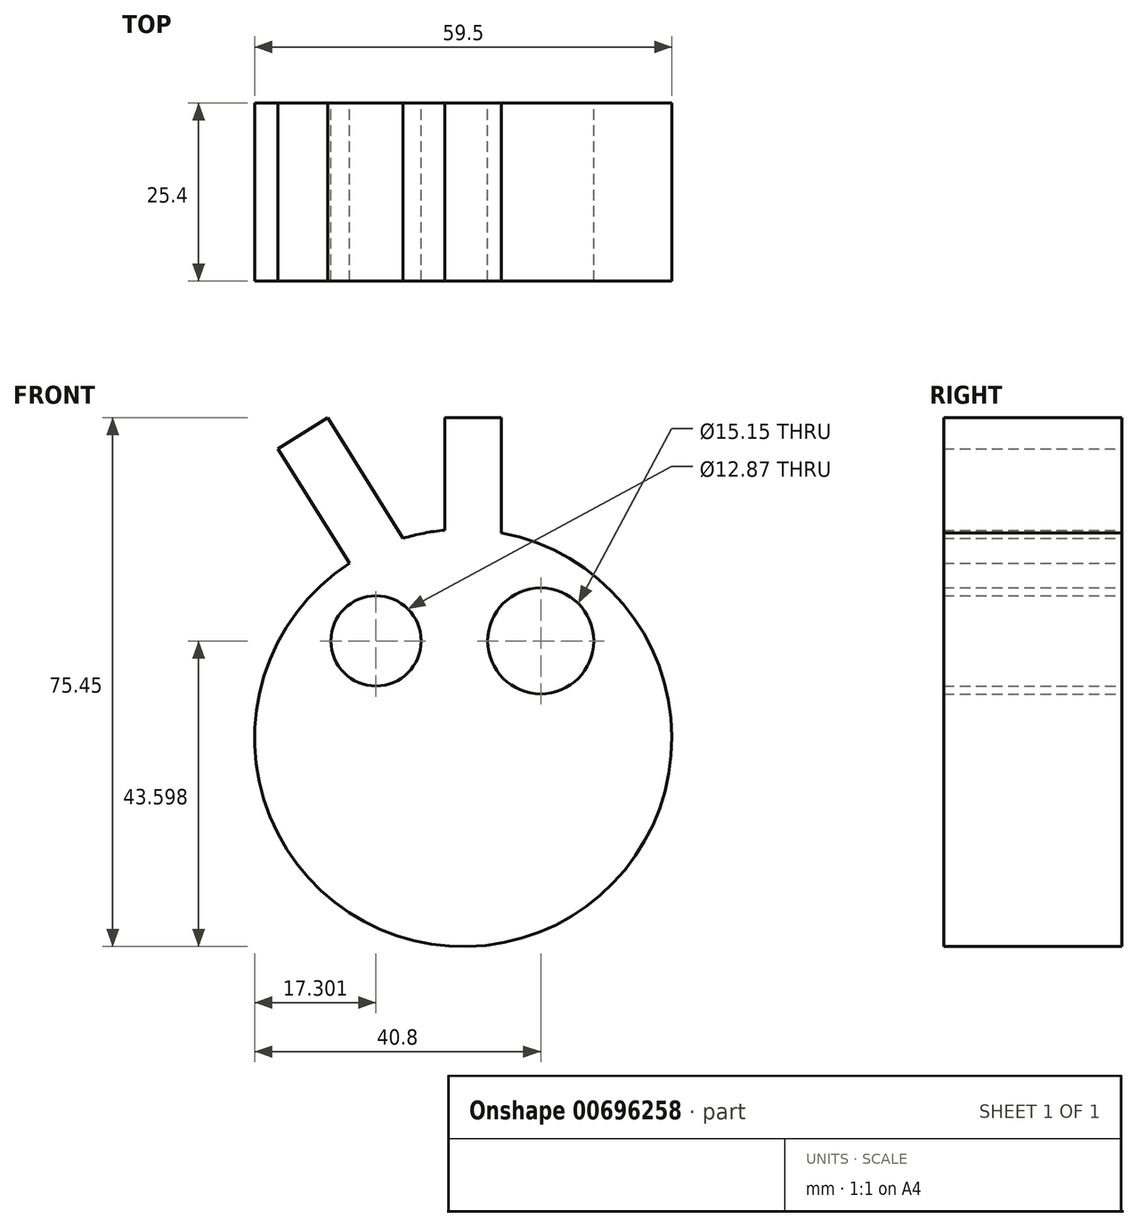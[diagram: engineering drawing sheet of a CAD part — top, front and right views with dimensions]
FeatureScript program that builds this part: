
annotation { "Feature Type Name" : "Feature", "Feature Type Description" : "" }
export const myFeature = defineFeature(function(context is Context, id is Id, definition is map)
    precondition{}
    {
        {
            var Q0;
            Q0=qCreatedBy(makeId("Front.planeOp"),FACE);
            var sketch = newSketch(context, id + "F0", { "sketchPlane" : qUnion([Q0])});
            skCircle(sketch, "E0", {"center": v(0, 0) * mm, "radius": 29.75 * mm});
            skLineSegment(sketch, "E1", {"start": v(-16.23, 24.94) * mm, "end": v(-26.44, 41.26) * mm});
            skLineSegment(sketch, "E2", {"start": v(-26.44, 41.26) * mm, "end": v(-19.35, 45.7) * mm});
            skLineSegment(sketch, "E3", {"start": v(-19.35, 45.7) * mm, "end": v(-8.58, 28.49) * mm});
            skLineSegment(sketch, "E4", {"start": v(-8.58, 28.49) * mm, "end": v(-19.35, 45.7) * mm});
            skLineSegment(sketch, "E5", {"start": v(-2.63, 29.64) * mm, "end": v(-2.63, 45.7) * mm});
            skLineSegment(sketch, "E6", {"start": v(-2.63, 45.7) * mm, "end": v(5.46, 45.7) * mm});
            skLineSegment(sketch, "E7", {"start": v(5.46, 45.7) * mm, "end": v(5.46, 29.25) * mm});
            skLineSegment(sketch, "E8", {"start": v(5.46, 29.25) * mm, "end": v(5.46, 45.7) * mm});
            skCircle(sketch, "E9", {"center": v(-12.45, 13.85) * mm, "radius": 6.43 * mm});
            skCircle(sketch, "E10", {"center": v(11.05, 13.85) * mm, "radius": 7.57 * mm});
            skArc(sketch, "E11", {"start": v(-10.77, -11.33) * mm, "mid": v(1.19, -20.75) * mm, "end": v(13.57, -11.89) * mm});
            skSolve(sketch);
        }
        {
            var Q0;
            Q0 = qSketchRegion(id + "F0", true);
            extrude(context, id + "F1", {"entities" : qUnion([Q0]), "depth" : 25.4 * mm, "offsetDistance" : 25.4 * mm});
        }
        {
            var Q0;
            Q0=qCreatedBy(makeId("Front.planeOp"),FACE);
            var sketch = newSketch(context, id + "F2", { "sketchPlane" : qUnion([Q0])});
            skLineSegment(sketch, "E12.bottom", {"start": v(-9.93, -9.1) * mm, "end": v(12.45, -9.1) * mm});
            skLineSegment(sketch, "E12.top", {"start": v(-9.93, -12.45) * mm, "end": v(12.45, -12.45) * mm});
            skLineSegment(sketch, "E12.left", {"start": v(-9.93, -9.1) * mm, "end": v(-9.93, -12.45) * mm});
            skLineSegment(sketch, "E12.right", {"start": v(12.45, -9.1) * mm, "end": v(12.45, -12.45) * mm});
            skLineSegment(sketch, "E13.bottom", {"start": v(-6.3, -9.1) * mm, "end": v(7.13, -9.1) * mm});
            skLineSegment(sketch, "E13.top", {"start": v(-6.3, -12.45) * mm, "end": v(7.13, -12.45) * mm});
            skLineSegment(sketch, "E13.left", {"start": v(-6.3, -9.1) * mm, "end": v(-6.3, -12.45) * mm});
            skLineSegment(sketch, "E13.right", {"start": v(7.13, -9.1) * mm, "end": v(7.13, -12.45) * mm});
            skLineSegment(sketch, "E14", {"start": v(0, 11.6) * mm, "end": v(-7.13, 0) * mm});
            skLineSegment(sketch, "E15", {"start": v(-7.13, 0) * mm, "end": v(0, 0) * mm});
            skLineSegment(sketch, "E16", {"start": v(0, 0) * mm, "end": v(0, 11.6) * mm});
            skLineSegment(sketch, "E17", {"start": v(0, 0) * mm, "end": v(-7.13, 0) * mm});
            skLineSegment(sketch, "E18", {"start": v(0, 11.6) * mm, "end": v(0, 0) * mm});
            skSolve(sketch);
        }
        {
            var Q0;
            Q0 = qSketchRegion(id + "F2", true);
            extrude(context, id + "F3", {"entities" : qUnion([Q0]), "operationType" : NewBodyOperationType.ADD, "depth" : 25.4 * mm, "offsetDistance" : 25.4 * mm});
        }
    });
